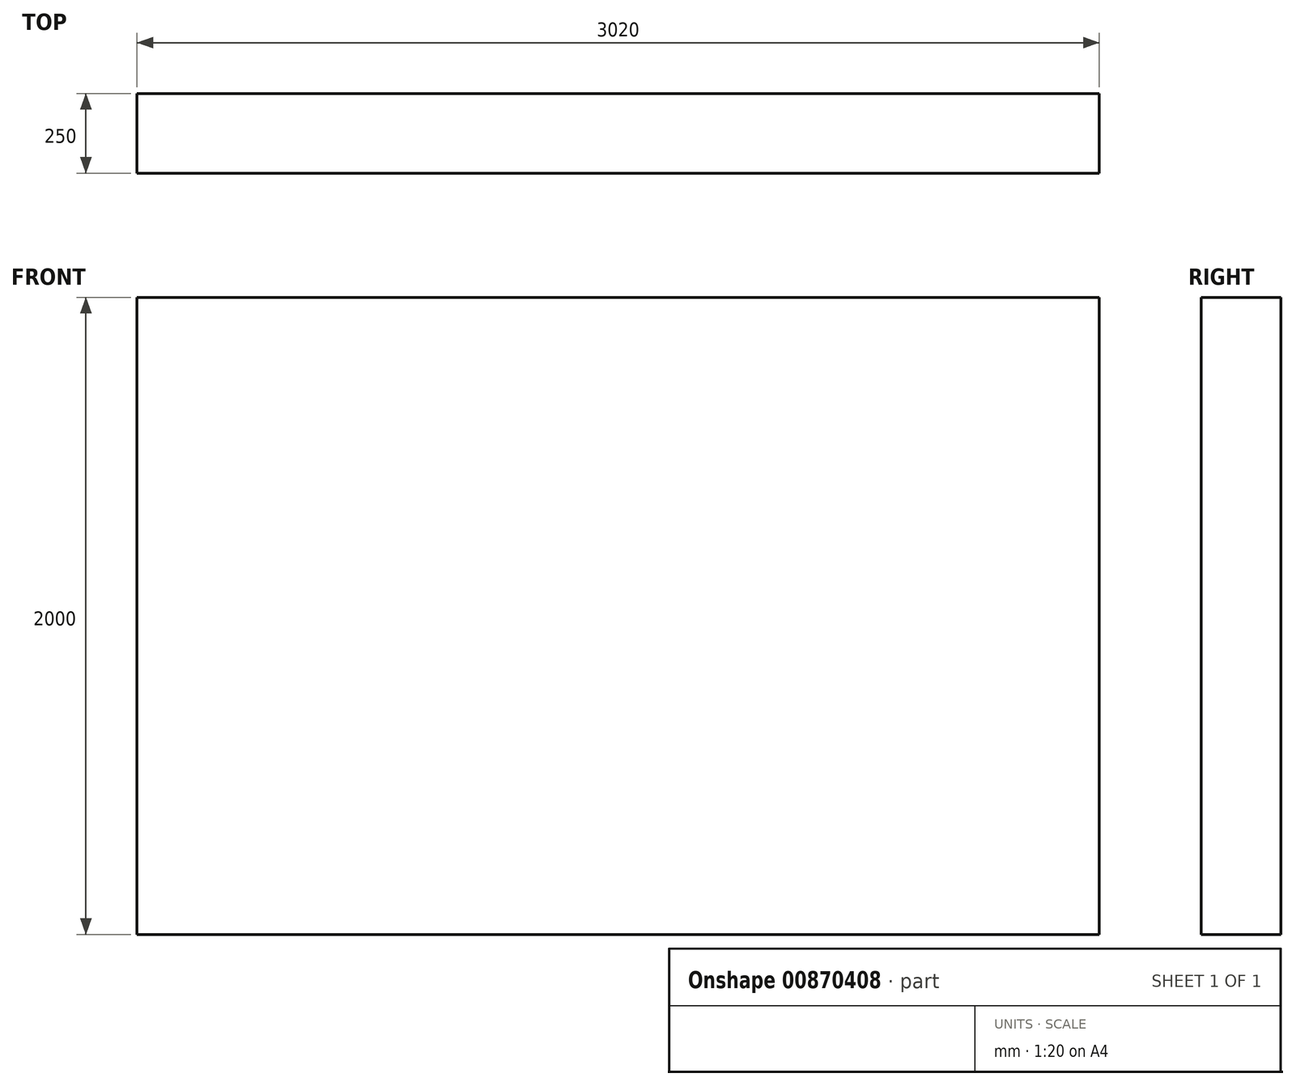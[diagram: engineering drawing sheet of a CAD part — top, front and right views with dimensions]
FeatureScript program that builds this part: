
annotation { "Feature Type Name" : "Feature", "Feature Type Description" : "" }
export const myFeature = defineFeature(function(context is Context, id is Id, definition is map)
    precondition{}
    {
        {
            var Q0;
            Q0=qCreatedBy(makeId("Front.planeOp"),FACE);
            var sketch = newSketch(context, id + "F0", { "sketchPlane" : qUnion([Q0])});
            skLineSegment(sketch, "E0.bottom", {"start": v(1510, 1000) * mm, "end": v(-1510, 1000) * mm});
            skLineSegment(sketch, "E0.top", {"start": v(1510, -1000) * mm, "end": v(-1510, -1000) * mm});
            skLineSegment(sketch, "E0.left", {"start": v(1510, 1000) * mm, "end": v(1510, -1000) * mm});
            skLineSegment(sketch, "E0.right", {"start": v(-1510, 1000) * mm, "end": v(-1510, -1000) * mm});
            skPoint(sketch, "E0.middle", {"position": v(0, 0) * mm});
            skSolve(sketch);
        }
        {
            var Q0;
            Q0=makeQuery(id+"F0.imprint","IMPRINT",FACE,{"disambiguationData":[TD([[makeQuery(id+"F0.imprint","IMPRINT",EDGE,{"derivedFrom":sQuery(id+"F0.wireOp",EDGE,"E0.bottom")}),1.0]])]});
            extrude(context, id + "F1", {"entities" : qUnion([Q0]), "oppositeDirection" : true, "depth" : 250 * mm, "offsetDistance" : 25 * mm});
        }
    });
